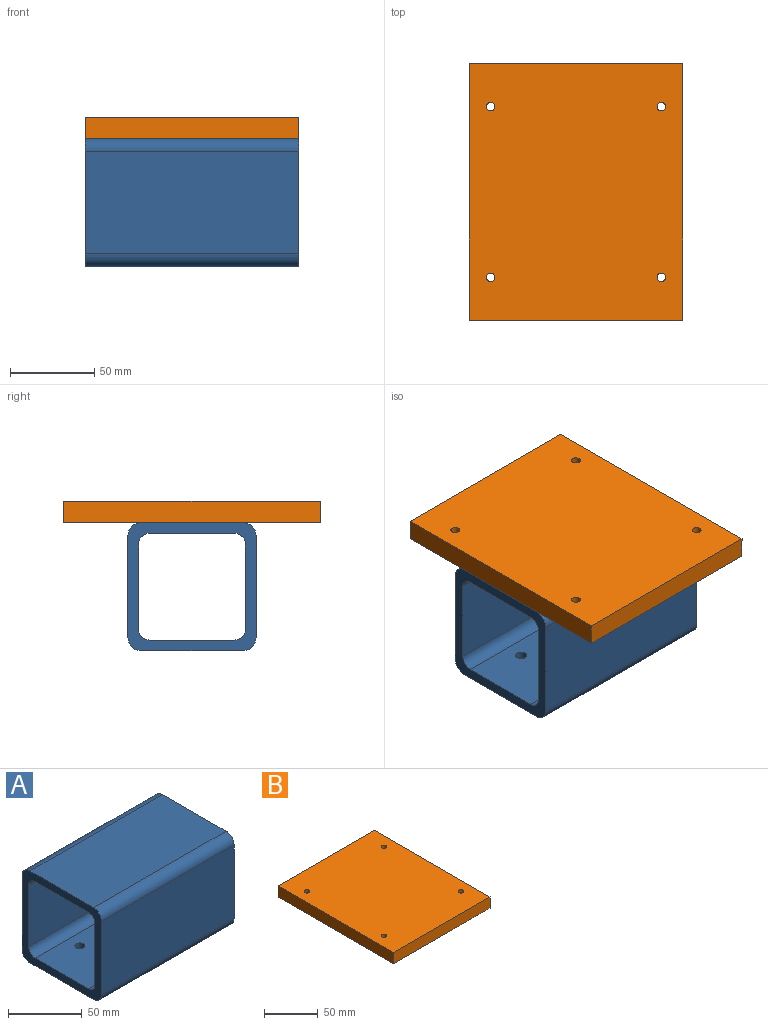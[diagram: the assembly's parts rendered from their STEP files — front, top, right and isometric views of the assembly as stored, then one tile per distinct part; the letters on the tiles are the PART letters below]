
ASSEMBLY  parts=2 mates=1
PART A: 22 faces, bbox 127x76.2x76.2 mm
  f0: plane 127x60.96mm, normal (0,1,0), area 7741.9mm2, adj f1,f15,f16,f17
  f1: cylinder r=7.62mm len=127mm, axis (-1,0,0), area 1520.1mm2, adj f0,f2,f16,f17
  f2: plane 127x60.96mm, normal (0,0,1), area 7741.9mm2, adj f1,f3,f16,f17
  f3: cylinder r=7.62mm len=127mm, axis (-1,0,0), area 1520.1mm2, adj f2,f4,f16,f17
  f4: plane 127x60.96mm, normal (0,-1,0), area 7741.9mm2, adj f3,f5,f16,f17
  f5: cylinder r=7.62mm len=127mm, axis (-1,0,0), area 1520.1mm2, adj f4,f6,f16,f17
  f6: plane 127x60.96mm, normal (0,0,-1), area 7598.6mm2, adj f5,f15,f16,f17,f18,f19,f20,f21
  f7: cylinder r=6.35mm len=127mm, axis (-1,0,0), area 1266.8mm2, adj f8,f14,f16,f17
  f8: plane 127x50.8mm, normal (0,0,-1), area 6451.6mm2, adj f7,f9,f16,f17
  f9: cylinder r=6.35mm len=127mm, axis (-1,0,0), area 1266.8mm2, adj f8,f10,f16,f17
  f10: plane 127x50.8mm, normal (0,-1,0), area 6451.6mm2, adj f9,f11,f16,f17
  f11: cylinder r=6.35mm len=127mm, axis (-1,0,0), area 1266.8mm2, adj f10,f12,f16,f17
  f12: plane 127x50.8mm, normal (0,0,1), area 6308.3mm2, adj f11,f13,f16,f17,f18,f19,f20,f21
  f13: cylinder r=6.35mm len=127mm, axis (-1,0,0), area 1266.8mm2, adj f12,f14,f16,f17
  f14: plane 127x50.8mm, normal (0,1,0), area 6451.6mm2, adj f7,f13,f16,f17
  f15: cylinder r=7.62mm len=127mm, axis (-1,0,0), area 1520.1mm2, adj f0,f6,f16,f17
  f16: plane 76.2x76.2mm, normal (1,0,0), area 1759mm2, adj f0,f1,f2,f3,f4,f5,f6,f7
  f17: plane 76.2x76.2mm, normal (-1,0,0), area 1759mm2, adj f0,f1,f2,f3,f4,f5,f6,f7
  f18: cylinder r=3.38mm len=6.76mm, axis (0,0,-1), area 134.8mm2, adj f6,f12
  f19: cylinder r=3.38mm len=6.76mm, axis (0,0,-1), area 134.8mm2, adj f6,f12
  f20: cylinder r=3.37mm len=6.75mm, axis (0,0,-1), area 134.6mm2, adj f6,f12
  f21: cylinder r=3.38mm len=6.76mm, axis (0,0,-1), area 134.8mm2, adj f6,f12
PART B: 10 faces, bbox 127x152.4x12.7 mm
  f0: plane 127x12.7mm, normal (0,-1,0), area 1612.9mm2, adj f2,f3,f4,f5
  f1: plane 127x12.7mm, normal (0,1,0), area 1612.9mm2, adj f2,f3,f4,f5
  f2: plane 152.4x127mm, normal (0,0,1), area 19272.9mm2, adj f0,f1,f4,f5,f6,f7,f8,f9
  f3: plane 152.4x127mm, normal (0,0,-1), area 19272.9mm2, adj f0,f1,f4,f5,f6,f7,f8,f9
  f4: plane 152.4x12.7mm, normal (1,0,0), area 1935.5mm2, adj f0,f1,f2,f3
  f5: plane 152.4x12.7mm, normal (-1,0,0), area 1935.5mm2, adj f0,f1,f2,f3
  f6: cylinder r=2.55mm len=12.7mm, axis (0,0,-1), area 203.7mm2, adj f2,f3
  f7: cylinder r=2.55mm len=12.7mm, axis (0,0,-1), area 203.7mm2, adj f2,f3
  f8: cylinder r=2.55mm len=12.7mm, axis (0,0,-1), area 203.7mm2, adj f2,f3
  f9: cylinder r=2.55mm len=12.7mm, axis (0,0,-1), area 203.7mm2, adj f2,f3
PLACE A t=(-89.7,23.06,-44.32)mm
PLACE B rot(axis=(-1,0,0),180deg) t=(50,61.16,44.58)mm
MATE fastened B.f2 <-> A.f2  axis (0,0,-1) through (-26.2,-15.04,31.88)mm
